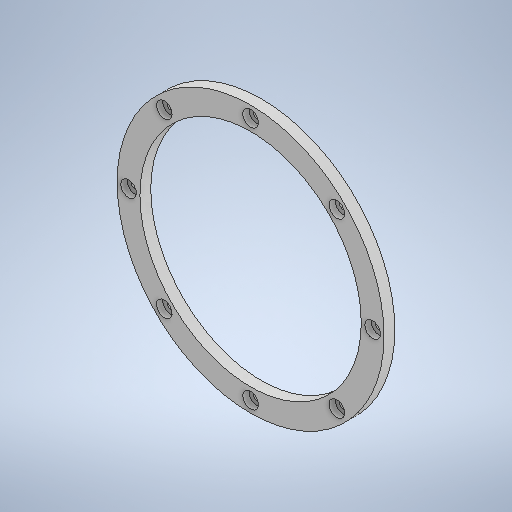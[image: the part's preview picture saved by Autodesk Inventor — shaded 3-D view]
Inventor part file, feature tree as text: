
AUTODESK INVENTOR PART (.ipt)
format: ipt  version: 2025 (Build 290162010, 162A)  size: 387,584 bytes
history: native  units: mm
features: extrude x5, sketch x5, other x2, pattern_circular x1, projected_geometry x1
ambient origin geometry x8: Origin, YZ Plane, XZ Plane, XY Plane, X Axis, Y Axis, Z Axis, Center Point
bodies: Solid1 (feature_tree)
feature tree (14):
  extrude  "Extrusion1"  Depth=389.0mm
  extrude  "Extrusion2"  Depth=38.0mm
  extrude  "Extrusion3"  Depth=80.0mm TaperAngle=360.0deg
  pattern_circular  "Circular Pattern1"  [2 undecoded]
  extrude  "Extrusion4"  Depth=19.0mm TaperAngle=0.0deg
  extrude  "Extrusion5"  Depth=38.0mm
  other  "A-Side Definition"
  sketch  "Sketch1"  dims[d0=40.0mm d1=389.0mm]
  sketch  "Sketch2"  dims[d2=38.0mm d3=0.0mm d4=12.5mm]
  projected_geometry  "Projected Loop1"
  sketch  "Sketch3"  dims[d5=0.0mm d6=0.0mm d7=80.0mm d8=360.0deg]
  sketch  "Sketch4"  dims[d10=27.5mm]
  sketch  "Sketch5"  dims[d11=11.0mm d12=0.0mm d13=5.0mm d14=9.0mm d15=0.0mm d16=38.0mm d17=19.0mm d18=0.0mm d19=0.0mm]
  other  "Definition1"
note: 2 required parameter values undecoded (feature->parameter linkage not recoverable at this tier; creation-order binding heuristic only, values carry confidence <= 0.55)
